# Revit family: Gira_109103
name_source: partatom
category: Elektroinstallationen
revit_build: Autodesk Revit 2017 (Build: 20160225_1515(x64)
units: mm (PartAtom-declared; Revit-internal decimal feet)

## family parameters
Basisbauteil = Fläche
Beim Laden mit Abzugskörper schneiden = Nein
Bemaßung runder Anschluss = Durchmesser verwenden
Beschriftungsausrichtung beibehalten = Nein
Gemeinsam genutzt = Nein
Raumberechnungspunkt = Nein
Teiletyp = Normal

## types (1)
- Gira_109103
    BIM = https://media.stage.bim.site
    Beschreibung = Cov.fr.1g in.sp. Std55 PW,Gira Standard 55 cover frame with inscription space,pure white glossy,1-gang,Features:,- Shatter-proof.,- Spray-proof.,- Frames with transparent view window for inscription.,- Ideally suited for use in buildings in which the electrical installation must be identified and documented, for example in managerial centres, commercial operations, airports, companies, and hospitals.,,Notes :,- Not to be used with: seal kit IP44, surface-mounted housing with flat design, surface-mounted housing.
    Colour = White
    Data sheet = https://katalog.gira.de
    Degree of protection (IP) = IP20
    GTIN = 4010337091035
    HAN = 109103
    Halogen free = Ja
    Hersteller = Gira
    Label space/information surface = Ja
    Material = Plastic
    Material quality = Thermoplastic
    Mounting direction = Vertical
    Number of units = 1
    Number of units vertical = 1
    Productwebsite = http://katalog.gira.de
    RAL-number (akin) = 9010
    Suitable for built-in installation = Nein
    Suitable for floor box = Nein
    Suitable for flush-mounted installation = Ja
    Suitable for wall duct = Nein
    Surface finishing = Glossy
    Surface protection = Other
    Transparent = Nein
    Type of fastening = Clamp mounting
    Typname = Cov.fr. 1-g in.sp. Standard 55 p.white
    URL = https://www.gira.de
    Vorgabe-Ansicht = 1219 mm
    With hinged lid = Nein
    With mounting grid = Nein

## geometry (parser evidence)
native form markers: Sweep x2
no freeform markers — native parametric forms only
